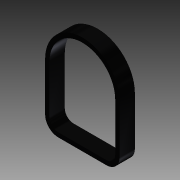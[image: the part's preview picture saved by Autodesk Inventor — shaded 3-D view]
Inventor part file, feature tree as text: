
AUTODESK INVENTOR PART (.ipt)
format: ipt  version: 2013 (Build 170138000, 138)  size: 111,104 bytes
history: native  units: in
note: dims shown in document units (in); Inventor stores cm internally (conversion verified against a paired STEP export)
features: reference x3, extrude x1, sketch x1
ambient origin geometry x8: Origin, YZ Plane, XZ Plane, XY Plane, X Axis, Y Axis, Z Axis, Center Point
bodies: Solid1 (feature_tree)
feature tree (5):
  extrude  "Extrusion1"  Depth=0.1378in TaperAngle=0.0deg
  sketch  "Sketch1"  dims[d0=0.0394in d3=0.1378in d4=0.0in]
  reference  "Reference1"
  reference  "Reference2"
  reference  "Reference3"
